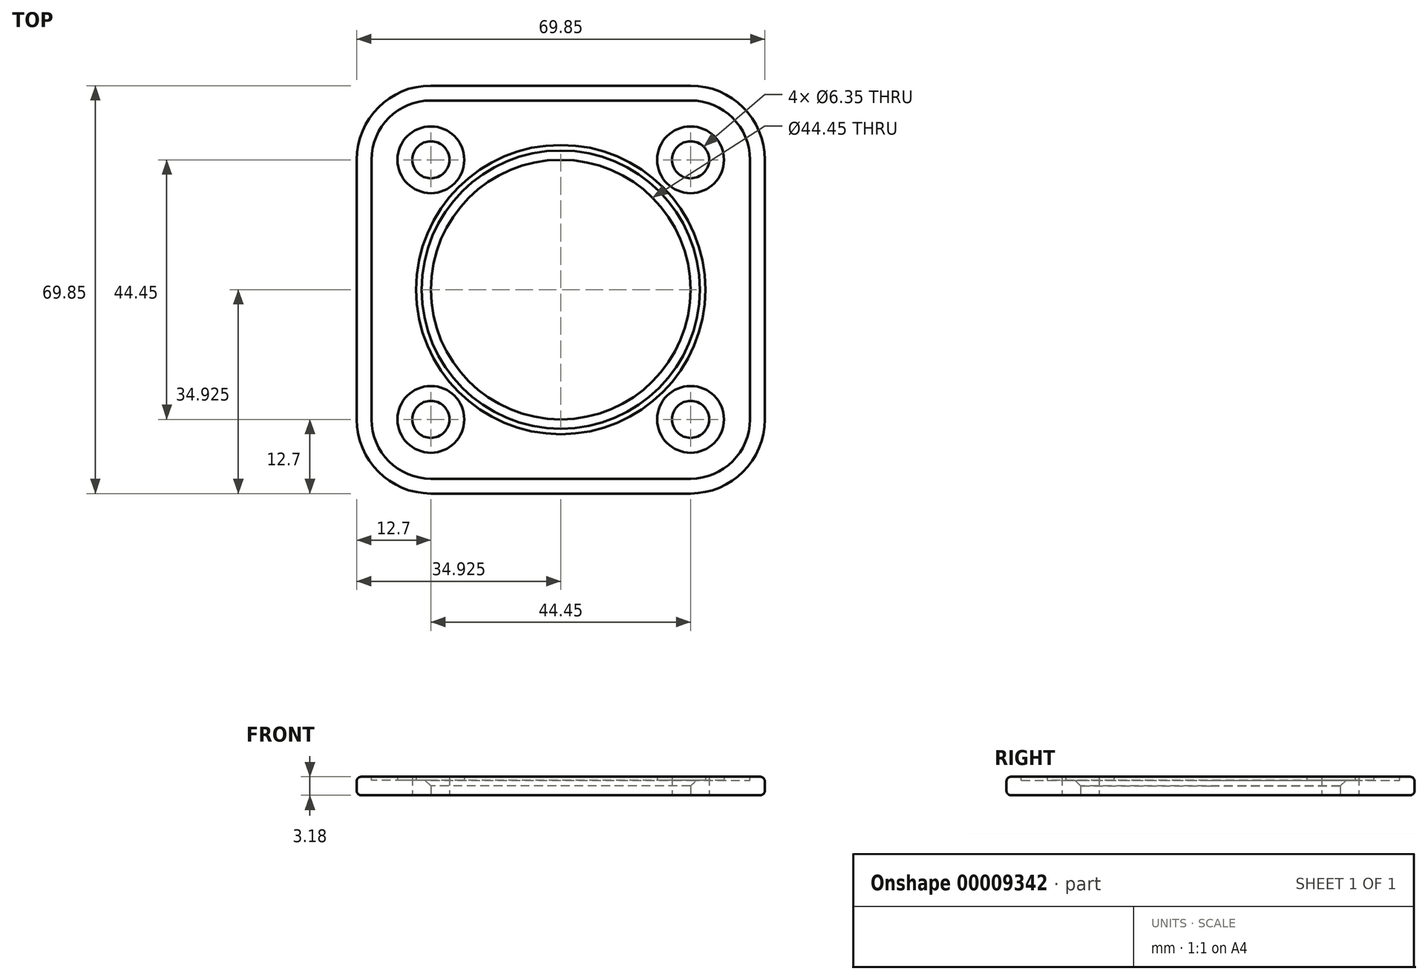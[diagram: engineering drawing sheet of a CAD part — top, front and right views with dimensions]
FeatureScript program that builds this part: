
annotation { "Feature Type Name" : "Feature", "Feature Type Description" : "" }
export const myFeature = defineFeature(function(context is Context, id is Id, definition is map)
    precondition{}
    {
        {
            var Q0;
            Q0=qCreatedBy(makeId("Top.planeOp"),FACE);
            var sketch = newSketch(context, id + "F4", { "sketchPlane" : qUnion([Q0])});
            skLineSegment(sketch, "E0.bottom", {"start": v(0, 0) * mm, "end": v(69.85, 0) * mm});
            skLineSegment(sketch, "E0.top", {"start": v(0, 69.85) * mm, "end": v(69.85, 69.85) * mm});
            skLineSegment(sketch, "E0.left", {"start": v(0, 0) * mm, "end": v(0, 69.85) * mm});
            skLineSegment(sketch, "E0.right", {"start": v(69.85, 0) * mm, "end": v(69.85, 69.85) * mm});
            skCircle(sketch, "E1", {"center": v(34.93, 34.92) * mm, "radius": 22.23 * mm});
            skPoint(sketch, "E2", {"position": v(69.85, 34.92) * mm});
            skPoint(sketch, "E3", {"position": v(34.93, 69.85) * mm});
            skCircle(sketch, "E4", {"center": v(12.7, 57.15) * mm, "radius": 3.18 * mm});
            skCircle(sketch, "E5", {"center": v(57.15, 57.15) * mm, "radius": 3.18 * mm});
            skCircle(sketch, "E6", {"center": v(57.15, 12.7) * mm, "radius": 3.18 * mm});
            skCircle(sketch, "E7", {"center": v(12.7, 12.7) * mm, "radius": 3.18 * mm});
            skSolve(sketch);
        }
        {
            var Q0;
            Q0=makeQuery(id+"F4.imprint","IMPRINT",FACE,{"disambiguationData":[TD([[makeQuery(id+"F4.imprint","IMPRINT",EDGE,{"derivedFrom":sQuery(id+"F4.wireOp",EDGE,"E0.bottom")}),1.0]])]});
            extrude(context, id + "F5", {"entities" : qUnion([Q0]), "depth" : 3.17 * mm});
        }
        {
            var Q0;
            Q0=makeQuery(id+"F5.opExtrude","SWEPT_EDGE",EDGE,{"disambiguationData":[OSD([sQuery(id+"F4.wireOp",EDGE,"E0.bottom"),sQuery(id+"F4.wireOp",EDGE,"E0.right")])]});
            var Q1;
            Q1=makeQuery(id+"F5.opExtrude","SWEPT_EDGE",EDGE,{"disambiguationData":[OSD([sQuery(id+"F4.wireOp",EDGE,"E0.top"),sQuery(id+"F4.wireOp",EDGE,"E0.right")])]});
            var Q2;
            Q2=makeQuery(id+"F5.opExtrude","SWEPT_EDGE",EDGE,{"disambiguationData":[OSD([sQuery(id+"F4.wireOp",EDGE,"E0.top"),sQuery(id+"F4.wireOp",EDGE,"E0.left")])]});
            var Q3;
            Q3=makeQuery(id+"F5.opExtrude","SWEPT_EDGE",EDGE,{"disambiguationData":[OSD([sQuery(id+"F4.wireOp",EDGE,"E0.bottom"),sQuery(id+"F4.wireOp",EDGE,"E0.left")])]});
            fillet(context, id + "F0", {"entities" : qUnion([Q0, Q1, Q2, Q3]), "radius" : 12.7 * mm, "tangentPropagation" : true, "allowEdgeOverflow" : false});
        }
        {
            var Q0;
            Q0=makeQuery(id+"F5.opExtrude","CAP_FACE",FACE,{"disambiguationData":[OSD([sQuery(id+"F4.wireOp",EDGE,"E0.bottom"),sQuery(id+"F4.wireOp",EDGE,"E0.top"),sQuery(id+"F4.wireOp",EDGE,"E0.left"),sQuery(id+"F4.wireOp",EDGE,"E0.right"),sQuery(id+"F4.wireOp",EDGE,"E1"),sQuery(id+"F4.wireOp",EDGE,"E4"),sQuery(id+"F4.wireOp",EDGE,"E5"),sQuery(id+"F4.wireOp",EDGE,"E6"),sQuery(id+"F4.wireOp",EDGE,"E7")])],"isStart":false});
            shell(context, id + "F1", {"entities" : qUnion([Q0]), "thickness" : 2.54 * mm});
        }
        {
            var Q0;
            Q0=makeQuery(id+"F5.opExtrude","CAP_EDGE",EDGE,{"disambiguationData":[OSD([sQuery(id+"F4.wireOp",EDGE,"E1")])],"isStart":false});
            chamfer(context, id + "F2", {"entities" : qUnion([Q0]), "width" : 1.59 * mm, "tangentPropagation" : true});
        }
        {
            var Q0;
            Q0=makeQuery(id+"F5.opExtrude","CAP_EDGE",EDGE,{"disambiguationData":[OSD([sQuery(id+"F4.wireOp",EDGE,"E0.bottom")])],"isStart":false});
            var Q1;
            Q1=makeQuery(id+"F5.opExtrude","CAP_EDGE",EDGE,{"disambiguationData":[OSD([sQuery(id+"F4.wireOp",EDGE,"E0.bottom")])],"isStart":true});
            fillet(context, id + "F3", {"entities" : qUnion([Q0, Q1]), "radius" : 0.8 * mm, "tangentPropagation" : true, "allowEdgeOverflow" : false});
        }
    });
